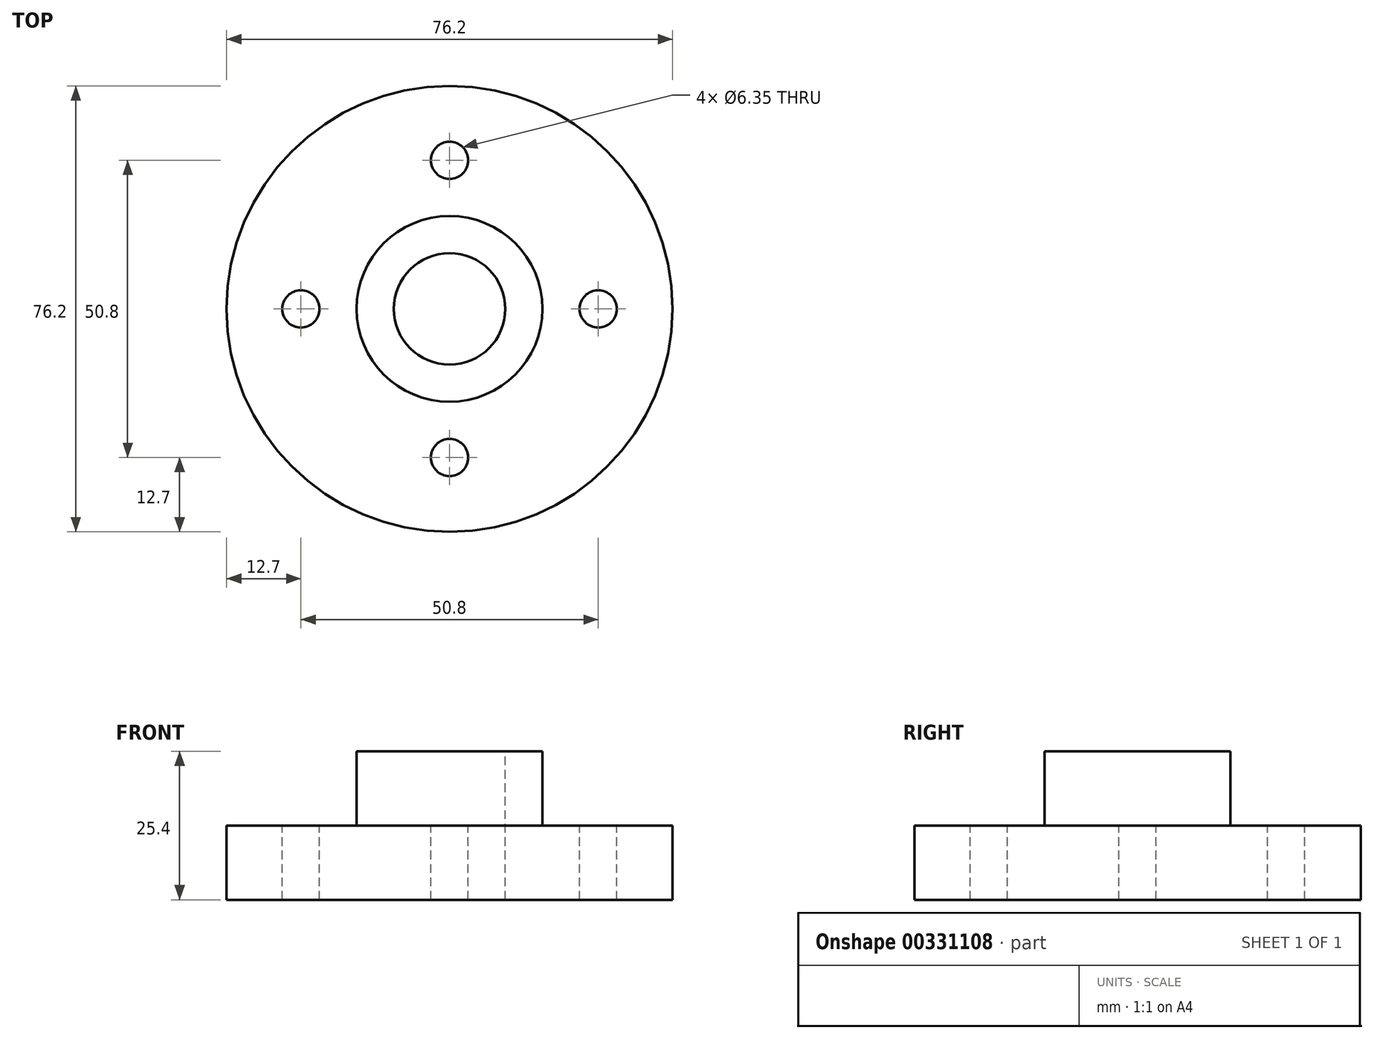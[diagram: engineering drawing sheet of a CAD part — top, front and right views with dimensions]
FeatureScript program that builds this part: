
annotation { "Feature Type Name" : "Feature", "Feature Type Description" : "" }
export const myFeature = defineFeature(function(context is Context, id is Id, definition is map)
    precondition{}
    {
        {
            var Q0;
            Q0=qCreatedBy(makeId("Top.planeOp"),FACE);
            var sketch = newSketch(context, id + "F0", { "sketchPlane" : qUnion([Q0])});
            skCircle(sketch, "E0", {"center": v(0, 0) * mm, "radius": 15.88 * mm});
            skCircle(sketch, "E1", {"center": v(0, 0) * mm, "radius": 38.1 * mm});
            skSolve(sketch);
        }
        {
            var Q0;
            Q0=makeQuery(id+"F0.imprint","IMPRINT",FACE,{"disambiguationData":[TD([[makeQuery(id+"F0.imprint","IMPRINT",EDGE,{"derivedFrom":sQuery(id+"F0.wireOp",EDGE,"E0")}),-1.0]])]});
            var Q1;
            Q1=makeQuery(id+"F0.imprint","IMPRINT",FACE,{"disambiguationData":[TD([[makeQuery(id+"F0.imprint","IMPRINT",EDGE,{"derivedFrom":sQuery(id+"F0.wireOp",EDGE,"E0")}),1.0]])]});
            extrude(context, id + "F1", {"entities" : qUnion([Q0, Q1]), "depth" : 12.7 * mm});
        }
        {
            var Q0;
            Q0=makeQuery(id+"F0.imprint","IMPRINT",FACE,{"disambiguationData":[TD([[makeQuery(id+"F0.imprint","IMPRINT",EDGE,{"derivedFrom":sQuery(id+"F0.wireOp",EDGE,"E0")}),1.0]])]});
            extrude(context, id + "F2", {"entities" : qUnion([Q0]), "operationType" : NewBodyOperationType.ADD, "depth" : 25.4 * mm});
        }
        {
            var Q0;
            Q0=makeQuery(id+"F2.opExtrude","CAP_FACE",FACE,{"disambiguationData":[OSD([sQuery(id+"F0.wireOp",EDGE,"E0")])],"isStart":false});
            var sketch = newSketch(context, id + "F3", { "sketchPlane" : qUnion([Q0])});
            skCircle(sketch, "E2", {"center": v(0, 0) * mm, "radius": 9.53 * mm});
            skSolve(sketch);
        }
        {
            var Q0;
            Q0=makeQuery(id+"F3.imprint","IMPRINT",FACE,{"disambiguationData":[TD([[makeQuery(id+"F3.imprint","IMPRINT",EDGE,{"derivedFrom":sQuery(id+"F3.wireOp",EDGE,"E2")}),1.0]])]});
            var Q1;
            Q1=makeQuery(id+"F1.opExtrude","CAP_FACE",FACE,{"disambiguationData":[OSD([sQuery(id+"F0.wireOp",EDGE,"E1")])],"isStart":true});
            extrude(context, id + "F4", {"entities" : qUnion([Q0]), "operationType" : NewBodyOperationType.REMOVE, "endBound" : BoundingType.UP_TO_SURFACE, "oppositeDirection" : true, "endBoundEntityFace" : qUnion([Q1]), "depth" : 25.4 * mm});
        }
        {
            var Q0;
            Q0=makeQuery(id+"F1.opExtrude","CAP_FACE",FACE,{"disambiguationData":[OSD([sQuery(id+"F0.wireOp",EDGE,"E1")])],"isStart":false});
            var sketch = newSketch(context, id + "F5", { "sketchPlane" : qUnion([Q0])});
            skLineSegment(sketch, "E3", {"start": v(-38.1, 0) * mm, "end": v(38.1, 0) * mm, "construction": true});
            skLineSegment(sketch, "E4", {"start": v(0, 38.1) * mm, "end": v(0, -38.1) * mm, "construction": true});
            skCircle(sketch, "E5", {"center": v(0, 0) * mm, "radius": 25.4 * mm, "construction": true});
            skPoint(sketch, "E6", {"position": v(0, 25.4) * mm});
            skPoint(sketch, "E7", {"position": v(25.4, 0) * mm});
            skPoint(sketch, "E8", {"position": v(0, -25.4) * mm});
            skPoint(sketch, "E9", {"position": v(-25.4, 0) * mm});
            skSolve(sketch);
        }
        {
            var Q0;
            Q0=sQuery(id+"F5.wireOp",VERTEX,"E6");
            var Q1;
            Q1=sQuery(id+"F5.wireOp",VERTEX,"E7");
            var Q2;
            Q2=sQuery(id+"F5.wireOp",VERTEX,"E8");
            var Q3;
            Q3=sQuery(id+"F5.wireOp",VERTEX,"E9");
            var Q4;
            Q4=makeQuery(id+"F1.opExtrude","SWEPT_BODY",BODY,{"disambiguationData":[OSD([sQuery(id+"F0.wireOp",EDGE,"E1")])]});
            hole(context, id + "F6", {"style" : HoleStyle.SIMPLE, "endStyle" : HoleEndStyle.THROUGH, "holeDiameter" : 6.35 * mm, "tappedDepth" : 12.7 * mm, "tapClearance" : 3, "locations" : qUnion([Q0, Q1, Q2, Q3]), "scope" : qUnion([Q4])});
        }
    });
